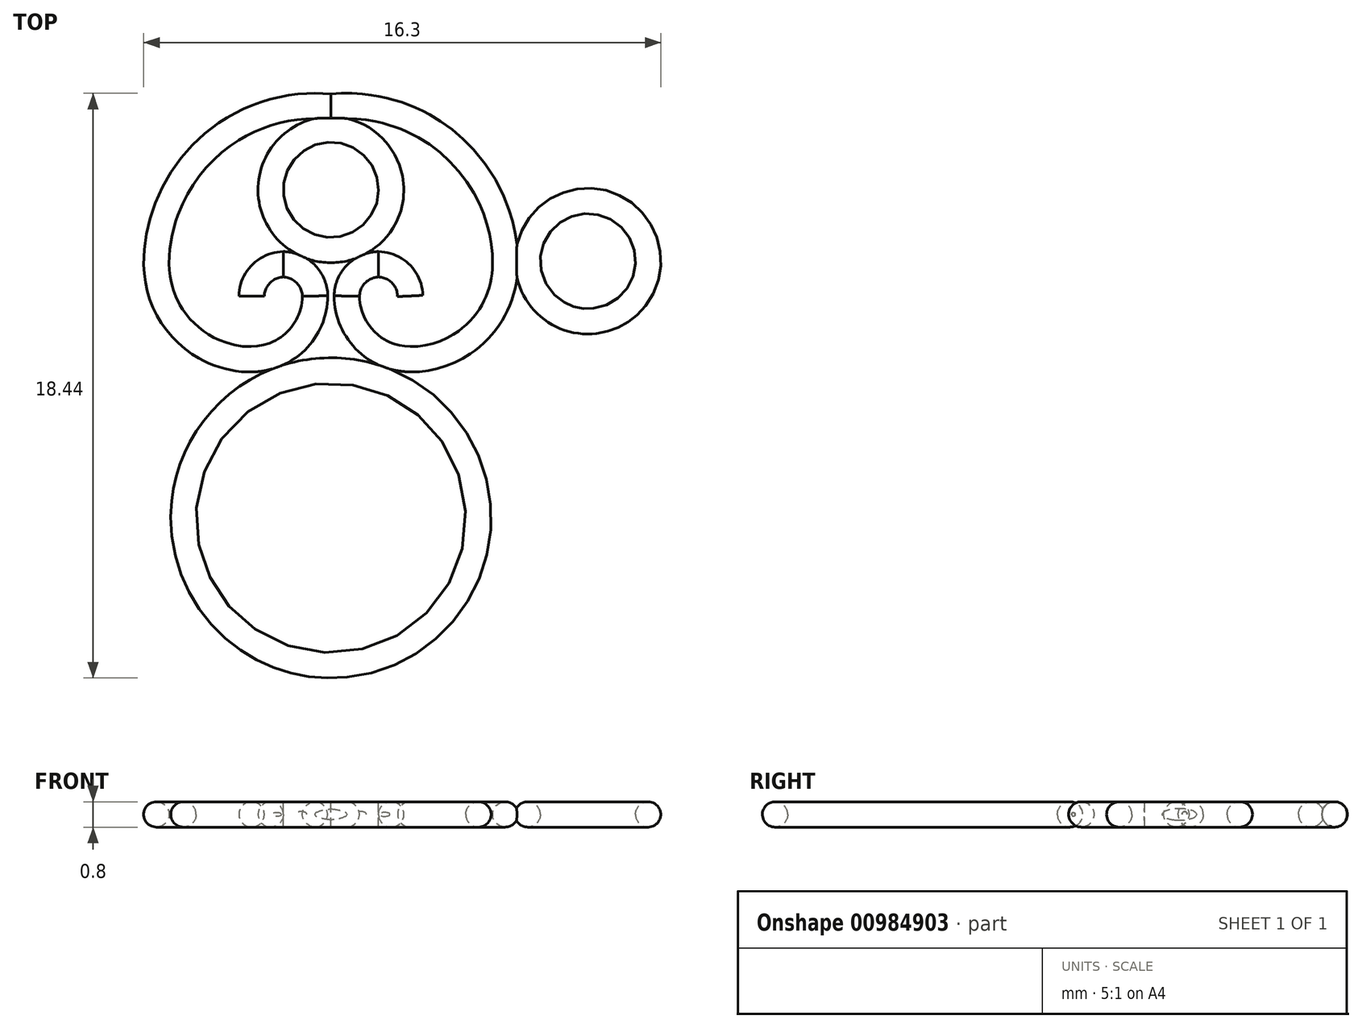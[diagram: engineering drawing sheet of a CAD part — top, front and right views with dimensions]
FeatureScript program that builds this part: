
annotation { "Feature Type Name" : "Feature", "Feature Type Description" : "" }
export const myFeature = defineFeature(function(context is Context, id is Id, definition is map)
    precondition{}
    {
        {
            var Q0;
            Q0=qCreatedBy(makeId("Top.planeOp"),FACE);
            var sketch = newSketch(context, id + "F0", { "sketchPlane" : qUnion([Q0])});
            skLineSegment(sketch, "E0.bottom", {"start": v(-0.5, 8) * mm, "end": v(-1.5, 8) * mm, "construction": true});
            skLineSegment(sketch, "E0.top", {"start": v(-0.5, 7) * mm, "end": v(-1.5, 7) * mm, "construction": true});
            skLineSegment(sketch, "E0.left", {"start": v(-0.5, 8) * mm, "end": v(-0.5, 7) * mm, "construction": true});
            skLineSegment(sketch, "E0.right", {"start": v(-1.5, 8) * mm, "end": v(-1.5, 7) * mm, "construction": true});
            skLineSegment(sketch, "E1.bottom", {"start": v(-1.5, 8) * mm, "end": v(-2.5, 8) * mm, "construction": true});
            skLineSegment(sketch, "E1.top", {"start": v(-1.5, 7) * mm, "end": v(-2.5, 7) * mm, "construction": true});
            skLineSegment(sketch, "E1.right", {"start": v(-2.5, 8) * mm, "end": v(-2.5, 7) * mm, "construction": true});
            skLineSegment(sketch, "E2.bottom", {"start": v(-2.5, 7) * mm, "end": v(0, 7) * mm, "construction": true});
            skLineSegment(sketch, "E2.top", {"start": v(-2.5, 5) * mm, "end": v(0, 5) * mm, "construction": true});
            skLineSegment(sketch, "E2.left", {"start": v(-2.5, 7) * mm, "end": v(-2.5, 5) * mm, "construction": true});
            skLineSegment(sketch, "E2.right", {"start": v(0, 7) * mm, "end": v(0, 5) * mm, "construction": true});
            skLineSegment(sketch, "E3.bottom", {"start": v(-2.5, 5) * mm, "end": v(-5.5, 5) * mm, "construction": true});
            skLineSegment(sketch, "E3.top", {"start": v(-2.5, 8) * mm, "end": v(-5.5, 8) * mm, "construction": true});
            skLineSegment(sketch, "E3.left", {"start": v(-2.5, 5) * mm, "end": v(-2.5, 8) * mm, "construction": true});
            skLineSegment(sketch, "E3.right", {"start": v(-5.5, 5) * mm, "end": v(-5.5, 8) * mm, "construction": true});
            skLineSegment(sketch, "E4.bottom", {"start": v(-5.5, 8) * mm, "end": v(0, 8) * mm, "construction": true});
            skLineSegment(sketch, "E4.top", {"start": v(-5.5, 12.97) * mm, "end": v(0, 12.97) * mm, "construction": true});
            skLineSegment(sketch, "E4.left", {"start": v(-5.5, 8) * mm, "end": v(-5.5, 12.97) * mm, "construction": true});
            skLineSegment(sketch, "E4.right", {"start": v(0, 8) * mm, "end": v(0, 12.97) * mm, "construction": true});
            skArc(sketch, "E5", {"start": v(-1.5, 8) * mm, "mid": v(-0.8, 7.7) * mm, "end": v(-0.5, 7) * mm});
            skArc(sketch, "E6", {"start": v(-0.5, 7) * mm, "mid": v(-1.09, 5.59) * mm, "end": v(-2.5, 5) * mm});
            skArc(sketch, "E7", {"start": v(-2.5, 5) * mm, "mid": v(-4.62, 5.88) * mm, "end": v(-5.5, 8) * mm});
            skArc(sketch, "E8", {"start": v(-5.5, 8) * mm, "mid": v(-3.85, 11.7) * mm, "end": v(0, 12.97) * mm});
            skArc(sketch, "E9.MirrorCS", {"start": v(0.5, 7) * mm, "mid": v(1.09, 5.59) * mm, "end": v(2.5, 5) * mm});
            skArc(sketch, "E10.MirrorCS", {"start": v(5.5, 8) * mm, "mid": v(3.85, 11.7) * mm, "end": v(0, 12.97) * mm});
            skArc(sketch, "E11.MirrorCS", {"start": v(2.5, 5) * mm, "mid": v(4.62, 5.88) * mm, "end": v(5.5, 8) * mm});
            skArc(sketch, "E12.MirrorCS", {"start": v(1.5, 8) * mm, "mid": v(0.8, 7.7) * mm, "end": v(0.5, 7) * mm});
            skArc(sketch, "E13", {"start": v(-1.5, 8) * mm, "mid": v(-2.2, 7.7) * mm, "end": v(-2.5, 7) * mm});
            skArc(sketch, "E14.MirrorCS", {"start": v(1.5, 8) * mm, "mid": v(2.2, 7.7) * mm, "end": v(2.5, 7) * mm});
            skSolve(sketch);
        }
        {
            var Q0;
            Q0=qCreatedBy(makeId("Right.planeOp"),FACE);
            cPlane(context, id + "F1", {"entities" : qUnion([Q0]), "cplaneType" : CPlaneType.OFFSET, "offset" : 1.5 * mm, "width" : 150 * mm, "height" : 150 * mm});
        }
        {
            var Q0;
            Q0=qCreatedBy(id+"F1.planeOp",FACE);
            var sketch = newSketch(context, id + "F2", { "sketchPlane" : qUnion([Q0])});
            skCircle(sketch, "E15", {"center": v(8, 0) * mm, "radius": 0.4 * mm});
            skSolve(sketch);
        }
        {
            var Q0;
            Q0=makeQuery(id+"F2.imprint","IMPRINT",FACE,{"disambiguationData":[TD([[makeQuery(id+"F2.imprint","IMPRINT",EDGE,{"derivedFrom":sQuery(id+"F2.wireOp",EDGE,"E15")}),1.0]])]});
            var Q1;
            Q1=sQuery(id+"F0.wireOp",EDGE,"E9.MirrorCS");
            var Q2;
            Q2=sQuery(id+"F0.wireOp",EDGE,"E12.MirrorCS");
            var Q3;
            Q3=sQuery(id+"F0.wireOp",EDGE,"E11.MirrorCS");
            var Q4;
            Q4=sQuery(id+"F0.wireOp",EDGE,"E10.MirrorCS");
            var Q5;
            Q5=sQuery(id+"F0.wireOp",EDGE,"E8");
            var Q6;
            Q6=sQuery(id+"F0.wireOp",EDGE,"E7");
            var Q7;
            Q7=sQuery(id+"F0.wireOp",EDGE,"E6");
            var Q8;
            Q8=sQuery(id+"F0.wireOp",EDGE,"E5");
            var Q9;
            Q9=sQuery(id+"F0.wireOp",EDGE,"E14.MirrorCS");
            var Q10;
            Q10=sQuery(id+"F0.wireOp",EDGE,"E13");
            sweep(context, id + "F3", {"profiles" : qUnion([Q0]), "path" : qUnion([Q1, Q2, Q3, Q4, Q5, Q6, Q7, Q8, Q9, Q10])});
        }
        {
            var Q0;
            Q0=qCreatedBy(makeId("Top.planeOp"),FACE);
            var sketch = newSketch(context, id + "F4", { "sketchPlane" : qUnion([Q0])});
            skCircle(sketch, "E16", {"center": v(0, 0) * mm, "radius": 4.65 * mm});
            skSolve(sketch);
        }
        {
            var Q0;
            Q0=qCreatedBy(makeId("Right.planeOp"),FACE);
            var sketch = newSketch(context, id + "F5", { "sketchPlane" : qUnion([Q0])});
            skCircle(sketch, "E17", {"center": v(4.65, 0) * mm, "radius": 0.4 * mm});
            skSolve(sketch);
        }
        {
            var Q0;
            Q0=makeQuery(id+"F5.imprint","IMPRINT",FACE,{"disambiguationData":[TD([[makeQuery(id+"F5.imprint","IMPRINT",EDGE,{"derivedFrom":sQuery(id+"F5.wireOp",EDGE,"E17")}),1.0]])]});
            var Q1;
            Q1=sQuery(id+"F4.wireOp",EDGE,"E16");
            sweep(context, id + "F6", {"operationType" : NewBodyOperationType.ADD, "profiles" : qUnion([Q0]), "path" : qUnion([Q1])});
        }
        {
            var Q0;
            Q0=qCreatedBy(makeId("Top.planeOp"),FACE);
            var sketch = newSketch(context, id + "F7", { "sketchPlane" : qUnion([Q0])});
            skCircle(sketch, "E18", {"center": v(0, 10.35) * mm, "radius": 2.3 * mm});
            skCircle(sketch, "E19", {"center": v(0, 10.35) * mm, "radius": 1.5 * mm});
            skCircle(sketch, "E20", {"center": v(8.1, 8.1) * mm, "radius": 2.3 * mm});
            skCircle(sketch, "E21", {"center": v(8.1, 8.1) * mm, "radius": 1.5 * mm});
            skSolve(sketch);
        }
        {
            var Q0;
            Q0 = qSketchRegion(id + "F7", true);
            var Q1;
            Q1=makeQuery(id+"F7.imprint","IMPRINT",FACE,{"disambiguationData":[TD([[makeQuery(id+"F7.imprint","IMPRINT",EDGE,{"derivedFrom":sQuery(id+"F7.wireOp",EDGE,"E20")}),1.0]])]});
            extrude(context, id + "F8", {"entities" : qUnion([Q0, Q1]), "operationType" : NewBodyOperationType.ADD, "depth" : .4 * mm, "offsetDistance" : 25 * mm, "hasSecondDirection" : true, "secondDirectionOppositeDirection" : true, "secondDirectionDepth" : .4 * mm});
        }
        {
            var Q0;
            Q0=makeQuery(id+"F8.opExtrude","CAP_EDGE",EDGE,{"disambiguationData":[OSD([sQuery(id+"F7.wireOp",EDGE,"E18")])],"isStart":true});
            var Q1;
            Q1=makeQuery(id+"F8.opExtrude","CAP_EDGE",EDGE,{"disambiguationData":[OSD([sQuery(id+"F7.wireOp",EDGE,"E19")])],"isStart":false});
            var Q2;
            Q2=makeQuery(id+"F8.opExtrude","CAP_EDGE",EDGE,{"disambiguationData":[OSD([sQuery(id+"F7.wireOp",EDGE,"E19")])],"isStart":true});
            var Q3;
            Q3=makeQuery(id+"F8.opExtrude","CAP_EDGE",EDGE,{"disambiguationData":[OSD([sQuery(id+"F7.wireOp",EDGE,"E18")])],"isStart":false});
            var Q4;
            Q4=makeQuery(id+"F8.opExtrude","CAP_EDGE",EDGE,{"disambiguationData":[OSD([sQuery(id+"F7.wireOp",EDGE,"E21")])],"isStart":false});
            var Q5;
            Q5=makeQuery(id+"F8.opExtrude","CAP_EDGE",EDGE,{"disambiguationData":[OSD([sQuery(id+"F7.wireOp",EDGE,"E20")])],"isStart":true});
            var Q6;
            Q6=makeQuery(id+"F8.opExtrude","CAP_EDGE",EDGE,{"disambiguationData":[OSD([sQuery(id+"F7.wireOp",EDGE,"E21")])],"isStart":true});
            var Q7;
            Q7=makeQuery(id+"F8.opExtrude","CAP_EDGE",EDGE,{"disambiguationData":[OSD([sQuery(id+"F7.wireOp",EDGE,"E20")])],"isStart":false});
            fillet(context, id + "F9", {"entities" : qUnion([Q0, Q1, Q2, Q3, Q4, Q5, Q6, Q7]), "radius" : .4 * mm, "tangentPropagation" : true, "allowEdgeOverflow" : false});
        }
    });
